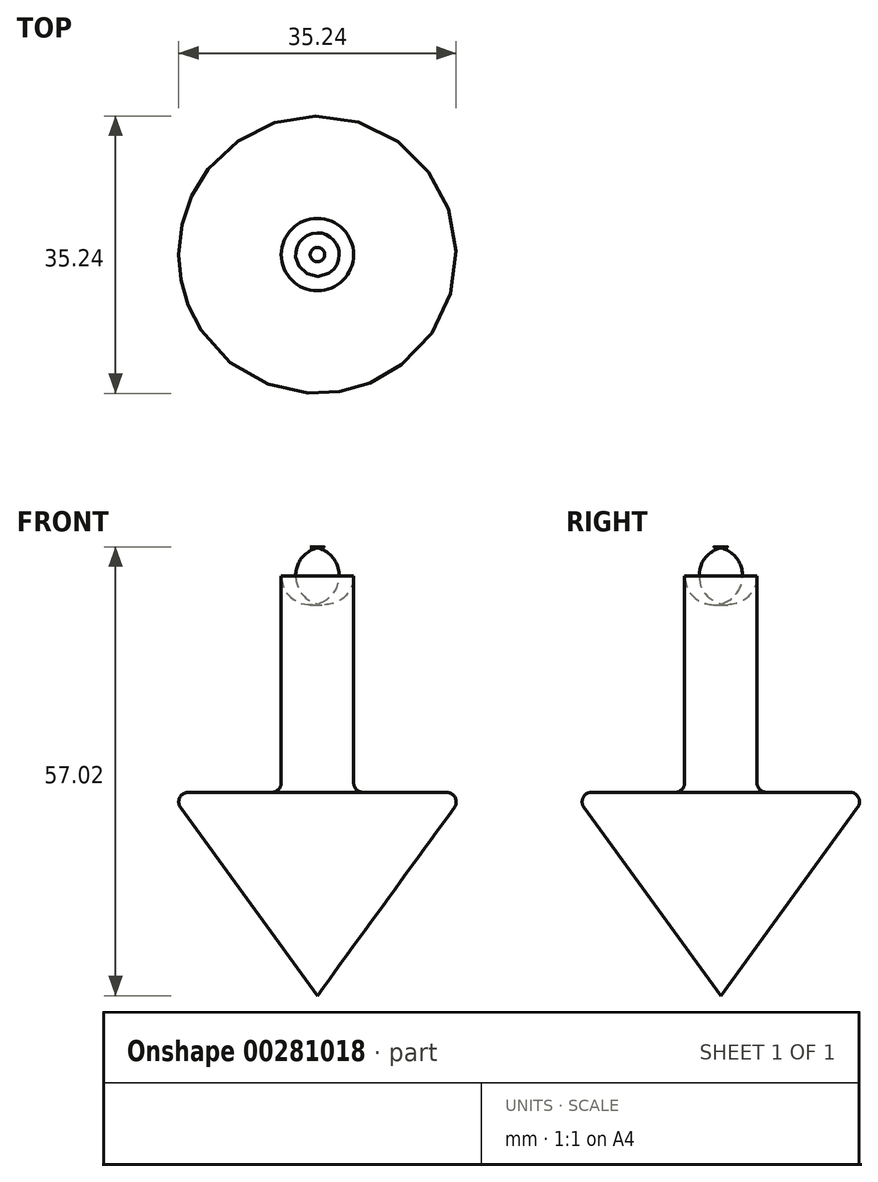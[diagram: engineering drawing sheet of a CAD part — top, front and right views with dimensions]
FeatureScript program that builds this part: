
annotation { "Feature Type Name" : "Feature", "Feature Type Description" : "" }
export const myFeature = defineFeature(function(context is Context, id is Id, definition is map)
    precondition{}
    {
        {
            var Q0;
            Q0=qCreatedBy(makeId("Front.planeOp"),FACE);
            var sketch = newSketch(context, id + "F0", { "sketchPlane" : qUnion([Q0])});
            skLineSegment(sketch, "E0", {"start": v(0, 0) * mm, "end": v(0, 57.02) * mm});
            skLineSegment(sketch, "E1", {"start": v(0, 57.02) * mm, "end": v(4.6, 57.02) * mm});
            skLineSegment(sketch, "E2", {"start": v(4.6, 57.02) * mm, "end": v(4.6, 25.84) * mm});
            skLineSegment(sketch, "E3", {"start": v(4.6, 25.84) * mm, "end": v(18.8, 25.84) * mm});
            skLineSegment(sketch, "E4", {"start": v(18.8, 25.84) * mm, "end": v(0, 0) * mm});
            skSolve(sketch);
        }
        {
            var Q0;
            Q0=makeQuery(id+"F0.imprint","IMPRINT",FACE,{"disambiguationData":[TD([[makeQuery(id+"F0.imprint","IMPRINT",EDGE,{"derivedFrom":sQuery(id+"F0.wireOp",EDGE,"E0")}),-1.0]])]});
            var Q1;
            Q1=sQuery(id+"F0.wireOp",EDGE,"E0");
            revolve(context, id + "F1", {"entities" : qUnion([Q0]), "axis" : qUnion([Q1]), "revolveType" : RevolveType.FULL});
        }
        {
            var Q0;
            Q0=makeQuery(id+"F1.opRevolve","SWEPT_EDGE",EDGE,{"disambiguationData":[OSD([sQuery(id+"F0.wireOp",EDGE,"E3"),sQuery(id+"F0.wireOp",EDGE,"E4")])]});
            var Q1;
            Q1=makeQuery(id+"F1.opRevolve","SWEPT_EDGE",EDGE,{"disambiguationData":[OSD([sQuery(id+"F0.wireOp",EDGE,"E2"),sQuery(id+"F0.wireOp",EDGE,"E3")])]});
            fillet(context, id + "F2", {"entities" : qUnion([Q0, Q1]), "radius" : 1.23 * mm, "tangentPropagation" : true, "allowEdgeOverflow" : false});
        }
        {
            var Q0;
            Q0=makeQuery(id+"F1.opRevolve","SWEPT_EDGE",EDGE,{"disambiguationData":[OSD([sQuery(id+"F0.wireOp",EDGE,"E1"),sQuery(id+"F0.wireOp",EDGE,"E2")])]});
            fillet(context, id + "F3", {"entities" : qUnion([Q0]), "radius" : 3.68 * mm, "tangentPropagation" : true, "allowEdgeOverflow" : false});
        }
    });
